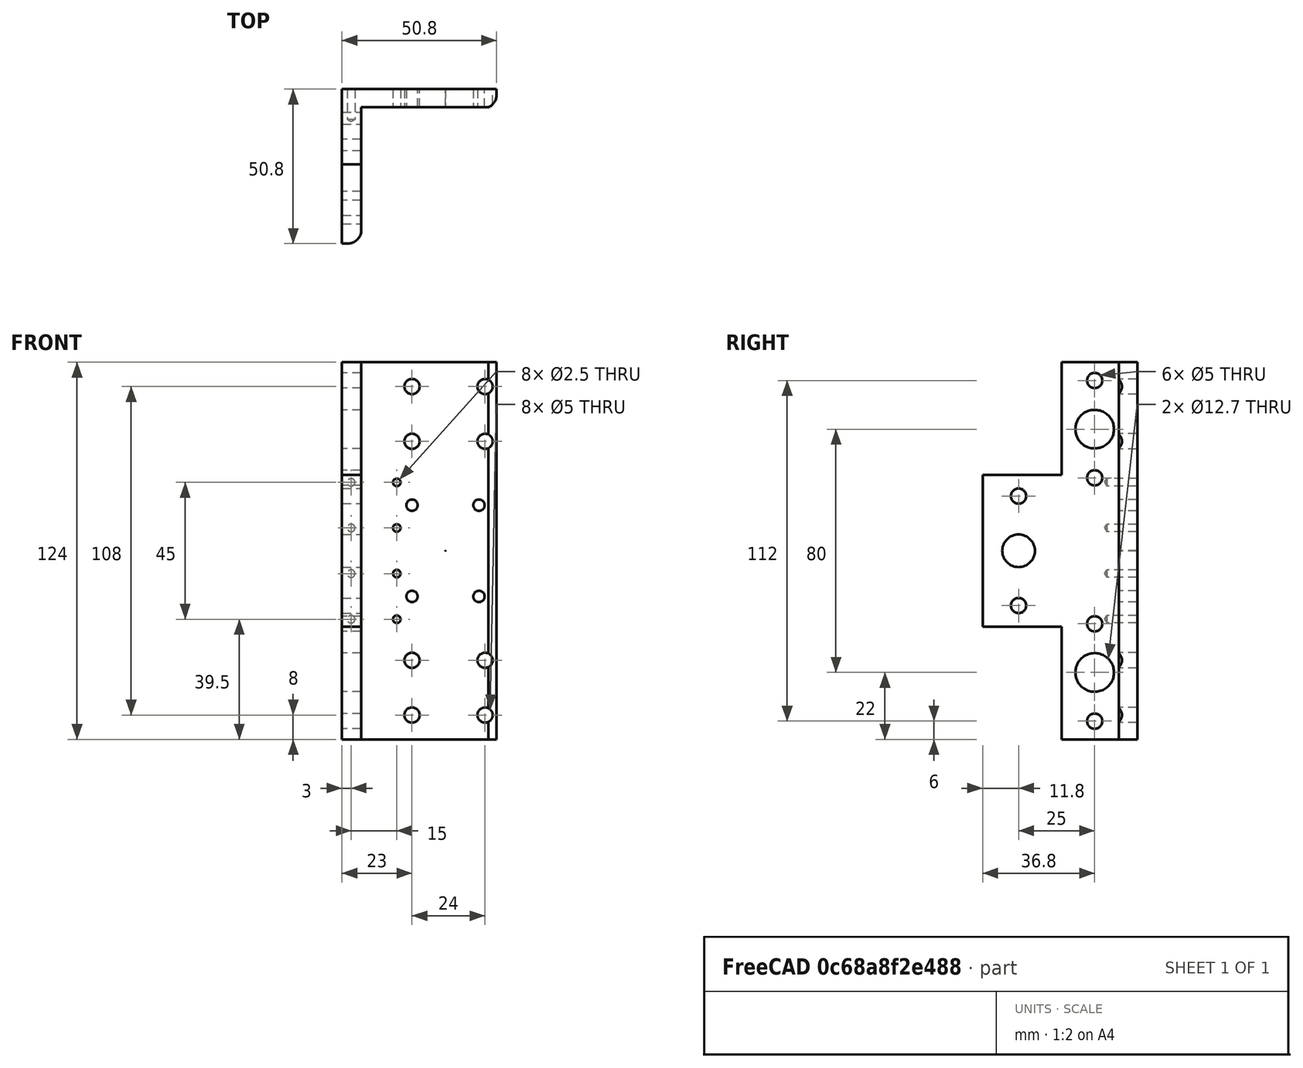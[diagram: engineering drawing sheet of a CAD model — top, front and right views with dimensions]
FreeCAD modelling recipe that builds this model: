
FCSTD DOCUMENT  (FreeCAD 0.19R)
Label: angle_machined_2in_25_drive_side
License: All rights reserved
LicenseURL: http://en.wikipedia.org/wiki/All_rights_reserved
objects: TechDraw::DrawViewDimension×26, PartDesign::CoordinateSystem×17, Sketcher::SketchObject×9, PartDesign::Pocket×7, PartDesign::Mirrored×3, TechDraw::DrawViewPart×3, PartDesign::Pad×2, PartDesign::Fillet×1, PartDesign::LinearPattern×1, PartDesign::Hole×1, PartDesign::Body×1, TechDraw::DrawSVGTemplate×1, TechDraw::DrawViewAnnotation×1, TechDraw::DrawPage×1
note: 53 computed .brp shape members not serialized (recipe doc carries the construction recipe); baked Part::Feature solids carry a one-line shape summary decoded from their .brp

FEATURE [Sketcher::SketchObject] Sketch
  FullyConstrained = true
  MapMode = 5
  Support = -> [XY_Plane]
  sketch-geometry (6):
    g0: LineSegment StartX=0 StartY=0 StartZ=0 EndX=50.8 EndY=0 EndZ=0
    g1: LineSegment StartX=50.8 StartY=0 StartZ=0 EndX=50.8 EndY=-6.35 EndZ=0
    g2: LineSegment StartX=50.8 StartY=-6.35 StartZ=0 EndX=6.35 EndY=-6.35 EndZ=0
    g3: LineSegment StartX=6.35 StartY=-6.35 StartZ=0 EndX=6.35 EndY=-50.8 EndZ=0
    g4: LineSegment StartX=6.35 StartY=-50.8 StartZ=0 EndX=0 EndY=-50.8 EndZ=0
    g5: LineSegment StartX=0 StartY=-50.8 StartZ=0 EndX=0 EndY=0 EndZ=0
  constraints (17):
    c: Coincident(g-1,g0)
    c: PointOnObject(g0,g-1)
    c: Coincident(g0,g1)
    c: Vertical(g1)
    c: Coincident(g1,g2)
    c: Horizontal(g2)
    c: Coincident(g2,g3)
    c: Vertical(g3)
    c: Coincident(g3,g4)
    c: PointOnObject(g4,g-2)
    c: Horizontal(g4)
    c: Coincident(g4,g5)
    c: Coincident(g5,g0)
    c: Equal(g1,g4)
    c: DistanceY(g1,g1) = 6.35
    c: DistanceX(g0,g0) = 50.8
    c: Equal(g0,g5)
FEATURE [PartDesign::Pad] Pad
  Direction = (1,1,1)
  Length = 62
  Length2 = 100
  Profile = -> Sketch
  Refine = true
  Reversed = true
  Type = 0
FEATURE [Sketcher::SketchObject] Sketch001
  FullyConstrained = true
  MapMode = 5
  Placement = pos=(0,0,0) rot=(0.57735,0.57735,0.57735;2.0944rad)
  Support = -> [YZ_Plane]
  sketch-geometry (3):
    g0: Circle CenterX=-14 CenterY=-40 CenterZ=0 NormalX=0 NormalY=0 NormalZ=1 AngleXU=0 Radius=6.35
    g1: Circle CenterX=-14 CenterY=-24 CenterZ=0 NormalX=0 NormalY=0 NormalZ=1 AngleXU=0 Radius=2.5
    g2: Circle CenterX=-14 CenterY=-56 CenterZ=0 NormalX=0 NormalY=0 NormalZ=1 AngleXU=0 Radius=2.5
  constraints (8):
    c: Diameter(g0) = 12.7
    c: Diameter(g1) = 5
    c: Equal(g1,g2)
    c: Symmetric(g1,g2,g0)
    c: Vertical(g1,g0)
    c: Distance(g1,g2) = 32
    c: DistanceX(g0,g-1) = 14
    c: DistanceY(g0,g-1) = 40
FEATURE [Sketcher::SketchObject] Sketch002
  FullyConstrained = true
  MapMode = 5
  Placement = pos=(0,0,0) rot=(0.57735,0.57735,0.57735;2.0944rad)
  Support = -> [YZ_Plane]
  sketch-geometry (3):
    g0: Circle CenterX=-39 CenterY=0 CenterZ=0 NormalX=0 NormalY=0 NormalZ=1 AngleXU=0 Radius=5.35781
    g1: Circle CenterX=-39 CenterY=18 CenterZ=0 NormalX=0 NormalY=0 NormalZ=1 AngleXU=0 Radius=2.5
    g2: Circle CenterX=-39 CenterY=-18 CenterZ=0 NormalX=0 NormalY=0 NormalZ=1 AngleXU=0 Radius=2.5
  constraints (8):
    c: Diameter(g0) = 10.7156
    c: Horizontal(g0,g-1)
    c: Vertical(g1,g0)
    c: Diameter(g1) = 5
    c: Equal(g1,g2)
    c: Symmetric(g1,g2,g0)
    c: DistanceY(g2,g1) = 36
    c: DistanceX(g1,g-1) = 39
FEATURE [Sketcher::SketchObject] Sketch003
  FullyConstrained = true
  MapMode = 5
  Placement = pos=(0,0,0) rot=(1,0,0;1.5708rad)
  Support = -> [XZ_Plane]
  sketch-geometry (4):
    g0: LineSegment StartX=6.35 StartY=251.119 StartZ=0 EndX=66.35 EndY=251.119 EndZ=0
    g1: LineSegment StartX=66.35 StartY=251.119 StartZ=0 EndX=66.35 EndY=200 EndZ=0
    g2: LineSegment StartX=66.35 StartY=200 StartZ=0 EndX=6.35 EndY=200 EndZ=0
    g3: LineSegment StartX=6.35 StartY=200 StartZ=0 EndX=6.35 EndY=251.119 EndZ=0
  constraints (12):
    c: Coincident(g0,g1)
    c: Coincident(g1,g2)
    c: Coincident(g2,g3)
    c: Coincident(g3,g0)
    c: Horizontal(g0)
    c: Horizontal(g2)
    c: Vertical(g1)
    c: Vertical(g3)
    c: DistanceY(g3,g3) = 51.1187
    c: DistanceY(g-1,g2) = 200
    c: DistanceX(g0,g0) = 60
    c: DistanceX(g-1,g0) = 6.35
FEATURE [Sketcher::SketchObject] Sketch004
  FullyConstrained = true
  MapMode = 5
  Placement = pos=(0,0,0) rot=(1,0,0;1.5708rad)
  Support = -> [XZ_Plane]
  sketch-geometry (7):
    g0: Circle CenterX=45 CenterY=15 CenterZ=0 NormalX=0 NormalY=0 NormalZ=1 AngleXU=0 Radius=1.865
    g1: Circle CenterX=45 CenterY=-15 CenterZ=0 NormalX=0 NormalY=0 NormalZ=1 AngleXU=0 Radius=1.865
    g2: Circle CenterX=23 CenterY=15 CenterZ=0 NormalX=0 NormalY=0 NormalZ=1 AngleXU=0 Radius=1.865
    g3: Circle CenterX=23 CenterY=-15 CenterZ=0 NormalX=0 NormalY=0 NormalZ=1 AngleXU=0 Radius=1.865
    g4: LineSegment StartX=0 StartY=0 StartZ=0 EndX=-20.31 EndY=0 EndZ=0
    g5: LineSegment StartX=34 StartY=0 StartZ=0 EndX=34 EndY=70 EndZ=0
    g6: Circle CenterX=34 CenterY=0 CenterZ=0 NormalX=0 NormalY=0 NormalZ=1 AngleXU=0 Radius=0.05
  constraints (18):
    c: Horizontal(g4)
    c: Coincident(g4,g-1)
    c: Distance(g4) = 20.31
    c: Vertical(g5)
    c: Horizontal(g5,g-1)
    c: Symmetric(g2,g0,g5)
    c: Symmetric(g2,g3,g4)
    c: Symmetric(g0,g1,g4)
    c: DistanceX(g2,g0) = 22
    c: Equal(g2,g0)
    c: Equal(g1,g0)
    c: Equal(g1,g3)
    c: Diameter(g0) = 3.73
    c: DistanceY(g1,g0) = 30
    c: DistanceX(g-1,g5) = 34  'motor_x'
    c: DistanceY(g5,g5) = 70
    c: Coincident(g6,g5)
    c: Diameter(g6) = 0.1
FEATURE [PartDesign::Pad] Pad001
  BaseFeature = -> Pad
  Direction = (1,1,1)
  Length = 62
  Length2 = 100
  Profile = -> Sketch
  Refine = true
  Type = 0
FEATURE [PartDesign::Fillet] Fillet
  Base = -> Pad001 [Edge17,Edge18,Edge16]
  BaseFeature = -> Pad001
  Radius = 4.5
  Refine = true
  SupportTransform = false
FEATURE [PartDesign::Pocket] Pocket  label="top_bearing"
  BaseFeature = -> Fillet
  Length = 20
  Length2 = 100
  Profile = -> Sketch001
  Refine = true
  Reversed = true
  Type = 1
FEATURE [PartDesign::LinearPattern] LinearPattern  label="LinearPattern_lower_bearing"
  BaseFeature = -> Pocket
  Direction = -> Sketch001 [V_Axis]
  Length = 80
  Occurrences = 2
  Originals = -> [Pocket]
  Refine = true
FEATURE [PartDesign::Pocket] Pocket001  label="drive_hole_clearance"
  BaseFeature = -> LinearPattern
  Length = 5
  Length2 = 100
  Midplane = true
  Profile = -> Sketch002
  Refine = true
  Reversed = true
  Type = 1
FEATURE [PartDesign::Pocket] Pocket002  label="gross_cut"
  BaseFeature = -> Pocket001
  Length = 5
  Length2 = 100
  Midplane = true
  Profile = -> Sketch003
  Refine = true
  Type = 1
FEATURE [PartDesign::Mirrored] Mirrored001
  BaseFeature = -> Pocket002
  MirrorPlane = -> Sketch003 [H_Axis]
  Originals = -> [Pocket002]
  Refine = true
FEATURE [PartDesign::Pocket] Pocket003
  BaseFeature = -> Mirrored001
  Length = 5
  Length2 = 100
  Midplane = true
  Profile = -> Sketch004
  Type = 1
FEATURE [Sketcher::SketchObject] Sketch005
  FullyConstrained = true
  MapMode = 5
  Support = -> [XY_Plane]
  sketch-geometry (4):
    g0: LineSegment StartX=6.35 StartY=-6 StartZ=0 EndX=66.35 EndY=-6 EndZ=0
    g1: LineSegment StartX=66.35 StartY=-6 StartZ=0 EndX=66.35 EndY=-18.25 EndZ=0
    g2: LineSegment StartX=66.35 StartY=-18.25 StartZ=0 EndX=6.35 EndY=-18.25 EndZ=0
    g3: LineSegment StartX=6.35 StartY=-18.25 StartZ=0 EndX=6.35 EndY=-6 EndZ=0
  constraints (12):
    c: Coincident(g0,g1)
    c: Coincident(g1,g2)
    c: Coincident(g2,g3)
    c: Coincident(g3,g0)
    c: Horizontal(g0)
    c: Horizontal(g2)
    c: Vertical(g1)
    c: Vertical(g3)
    c: DistanceY(g1,g1) = 12.25
    c: DistanceX(g0,g0) = 60
    c: DistanceX(g-1,g0) = 6.35
    c: DistanceY(g0,g-1) = 6
FEATURE [PartDesign::Pocket] Pocket004
  BaseFeature = -> Pocket003
  Length = 5
  Length2 = 100
  Midplane = true
  Profile = -> Sketch005
  Refine = true
  Type = 1
FEATURE [Sketcher::SketchObject] Sketch006
  FullyConstrained = true
  MapMode = 5
  Placement = pos=(0,0,0) rot=(0.57735,0.57735,0.57735;2.0944rad)
  Support = -> [YZ_Plane]
  sketch-geometry (4):
    g0: LineSegment StartX=-62.1666 StartY=69.7638 StartZ=0 EndX=-24.8 EndY=69.7638 EndZ=0
    g1: LineSegment StartX=-24.8 StartY=69.7638 StartZ=0 EndX=-24.8 EndY=25 EndZ=0
    g2: LineSegment StartX=-24.8 StartY=25 StartZ=0 EndX=-62.1666 EndY=25 EndZ=0
    g3: LineSegment StartX=-62.1666 StartY=25 StartZ=0 EndX=-62.1666 EndY=69.7638 EndZ=0
  constraints (12):
    c: Coincident(g0,g1)
    c: Coincident(g1,g2)
    c: Coincident(g2,g3)
    c: Coincident(g3,g0)
    c: Horizontal(g0)
    c: Horizontal(g2)
    c: Vertical(g1)
    c: Vertical(g3)
    c: DistanceX(g0,g-1) = 24.8
    c: DistanceY(g-1,g1) = 25
    c: DistanceX(g2,g2) = 37.3666
    c: DistanceY(g3,g3) = 44.7638
FEATURE [PartDesign::Pocket] Pocket005
  BaseFeature = -> Pocket004
  Length = 5
  Length2 = 100
  Midplane = true
  Profile = -> Sketch006
  Refine = true
  Type = 1
FEATURE [PartDesign::Mirrored] Mirrored
  BaseFeature = -> Pocket005
  MirrorPlane = -> Sketch006 [H_Axis]
  Originals = -> [Pocket005]
  Refine = true
FEATURE [PartDesign::CoordinateSystem] Local_CS007  label="lcs_NUT"
  AttacherType = Attacher::AttachEngine3D
  MapMode = 11
  Placement = pos=(6.35,-39,1.81e-14) rot=(0.707107,0,0.707107;3.14159rad)
  Support = -> [Mirrored]
FEATURE [Sketcher::SketchObject] Sketch007
  FullyConstrained = true
  MapMode = 5
  Placement = pos=(0,0,0) rot=(1,0,0;1.5708rad)
  Support = -> [XZ_Plane]
  sketch-geometry (5):
    g0: Circle CenterX=23 CenterY=54 CenterZ=0 NormalX=0 NormalY=0 NormalZ=1 AngleXU=0 Radius=2.5
    g1: Circle CenterX=47 CenterY=54 CenterZ=0 NormalX=0 NormalY=0 NormalZ=1 AngleXU=0 Radius=2.5
    g2: Circle CenterX=47 CenterY=36 CenterZ=0 NormalX=0 NormalY=0 NormalZ=1 AngleXU=0 Radius=2.5
    g3: Circle CenterX=23 CenterY=36 CenterZ=0 NormalX=0 NormalY=0 NormalZ=1 AngleXU=0 Radius=2.5
    g4: GeomPoint X=35 Y=45 Z=0
  constraints (13):
    c: Vertical(g0,g3)
    c: Horizontal(g1,g0)
    c: Horizontal(g2,g3)
    c: Vertical(g2,g1)
    c: DistanceX(g0,g1) = 24
    c: DistanceY(g2,g1) = 18
    c: Equal(g1,g2)
    c: Equal(g2,g3)
    c: Equal(g3,g0)
    c: Diameter(g1) = 5
    c: Symmetric(g3,g1,g4)
    c: DistanceY(g-1,g4) = 45  'y1'
    c: DistanceX(g-1,g4) = 35  'x1'
FEATURE [PartDesign::Pocket] Pocket006  label="bearing_holes"
  BaseFeature = -> Mirrored
  Length = 5
  Length2 = 100
  Midplane = true
  Profile = -> Sketch007
  Refine = true
  Type = 1
FEATURE [PartDesign::Mirrored] Mirrored002
  BaseFeature = -> Pocket006
  MirrorPlane = -> Sketch007 [H_Axis]
  Originals = -> [Pocket006]
  Refine = true
FEATURE [PartDesign::CoordinateSystem] Local_CS
  AttacherType = Attacher::AttachEngine3D
  MapMode = 11
  Placement = pos=(47,0,54) rot=(0.57735,-0.57735,0.57735;2.0944rad)
  Support = -> [Mirrored002]
FEATURE [PartDesign::CoordinateSystem] Local_CS009
  AttacherType = Attacher::AttachEngine3D
  MapMode = 11
  Placement = pos=(23,0,-36) rot=(0.57735,-0.57735,0.57735;2.0944rad)
  Support = -> [Mirrored002]
FEATURE [PartDesign::CoordinateSystem] Local_CS010
  AttacherType = Attacher::AttachEngine3D
  MapMode = 11
  Placement = pos=(45,0,15) rot=(0.57735,-0.57735,0.57735;2.0944rad)
  Support = -> [Mirrored002]
FEATURE [PartDesign::CoordinateSystem] Local_CS011
  AttacherType = Attacher::AttachEngine3D
  MapMode = 11
  Placement = pos=(23,3.3e-15,-15) rot=(0.57735,-0.57735,0.57735;2.0944rad)
  Support = -> [Sketch004]
FEATURE [PartDesign::CoordinateSystem] Local_CS012
  AttacherType = Attacher::AttachEngine3D
  MapMode = 11
  Placement = pos=(47,0,-54) rot=(0.57735,-0.57735,0.57735;2.0944rad)
  Support = -> [Mirrored002]
FEATURE [PartDesign::CoordinateSystem] Local_CS013
  AttacherType = Attacher::AttachEngine3D
  MapMode = 11
  Placement = pos=(23,0,15) rot=(0.57735,-0.57735,0.57735;2.0944rad)
  Support = -> [Mirrored002]
FEATURE [PartDesign::CoordinateSystem] Local_CS015
  AttacherType = Attacher::AttachEngine3D
  MapMode = 11
  Placement = pos=(6.35,-14,56) rot=(0.707107,0,-0.707107;3.14159rad)
  Support = -> [Mirrored002]
FEATURE [PartDesign::CoordinateSystem] Local_CS016
  AttacherType = Attacher::AttachEngine3D
  MapMode = 11
  Placement = pos=(6.35,-14,24) rot=(0.707107,0,-0.707107;3.14159rad)
  Support = -> [Mirrored002]
FEATURE [PartDesign::CoordinateSystem] Local_CS017
  AttacherType = Attacher::AttachEngine3D
  MapMode = 11
  Placement = pos=(6.35,-14,-24) rot=(0.707107,0,-0.707107;3.14159rad)
  Support = -> [Mirrored002]
FEATURE [PartDesign::CoordinateSystem] Local_CS018
  AttacherType = Attacher::AttachEngine3D
  MapMode = 11
  Placement = pos=(6.35,-14,-56) rot=(0.707107,0,-0.707107;3.14159rad)
  Support = -> [Mirrored002]
FEATURE [PartDesign::CoordinateSystem] Local_CS019
  AttacherType = Attacher::AttachEngine3D
  MapMode = 11
  Placement = pos=(-1.8e-14,-14,56) rot=(0.707107,0,0.707107;3.14159rad)
  Support = -> [Mirrored002]
FEATURE [PartDesign::CoordinateSystem] Local_CS020
  AttacherType = Attacher::AttachEngine3D
  MapMode = 11
  Placement = pos=(-1.8e-14,-14,24) rot=(0.707107,0,0.707107;3.14159rad)
  Support = -> [Mirrored002]
FEATURE [PartDesign::CoordinateSystem] Local_CS021
  AttacherType = Attacher::AttachEngine3D
  MapMode = 11
  Placement = pos=(0,-14,-24) rot=(0.707107,0,0.707107;3.14159rad)
  Support = -> [Mirrored002]
FEATURE [PartDesign::CoordinateSystem] Local_CS022
  AttacherType = Attacher::AttachEngine3D
  MapMode = 11
  Placement = pos=(0,-14,-56) rot=(0.707107,0,0.707107;3.14159rad)
  Support = -> [Mirrored002]
FEATURE [Sketcher::SketchObject] Sketch008
  FullyConstrained = true
  MapMode = 5
  Placement = pos=(0,0,0) rot=(0,0.707107,0.707107;3.14159rad)
  Support = -> [Mirrored002]
  sketch-geometry (8):
    g0: Circle CenterX=-18 CenterY=-7.5 CenterZ=0 NormalX=0 NormalY=0 NormalZ=1 AngleXU=0 Radius=1
    g1: Circle CenterX=-3 CenterY=-7.5 CenterZ=0 NormalX=0 NormalY=0 NormalZ=1 AngleXU=0 Radius=1
    g2: Circle CenterX=-3 CenterY=-22.5 CenterZ=0 NormalX=0 NormalY=0 NormalZ=1 AngleXU=0 Radius=1
    g3: Circle CenterX=-18 CenterY=-22.5 CenterZ=0 NormalX=0 NormalY=0 NormalZ=1 AngleXU=0 Radius=1
    g4: Circle CenterX=-3 CenterY=7.5 CenterZ=0 NormalX=0 NormalY=0 NormalZ=1 AngleXU=0 Radius=1
    g5: Circle CenterX=-3 CenterY=22.5 CenterZ=0 NormalX=0 NormalY=0 NormalZ=1 AngleXU=0 Radius=1
    g6: Circle CenterX=-18 CenterY=22.5 CenterZ=0 NormalX=0 NormalY=0 NormalZ=1 AngleXU=0 Radius=1
    g7: Circle CenterX=-18 CenterY=7.5 CenterZ=0 NormalX=0 NormalY=0 NormalZ=1 AngleXU=0 Radius=1
  constraints (20):
    c: Equal(g2,g1)
    c: Equal(g0,g1)
    c: Equal(g3,g0)
    c: DistanceX(g3,g2) = 15
    c: DistanceY(g2,g1) = 15
    c: Horizontal(g2,g3)
    c: Diameter(g0) = 2
    c: DistanceX(g1,g-1) = 3
    c: Horizontal(g1,g0)
    c: Vertical(g3,g0)
    c: Vertical(g1,g2)
    c: DistanceY(g1,g-1) = 7.5
    c: Symmetric(g1,g4,g-1)
    c: Symmetric(g0,g7,g-1)
    c: Symmetric(g2,g5,g-1)
    c: Symmetric(g6,g3,g-1)
    c: Equal(g4,g7)
    c: Equal(g5,g4)
    c: Equal(g5,g6)
    c: Equal(g3,g6)
FEATURE [PartDesign::Hole] Hole
  BaseFeature = -> Mirrored002
  Depth = 10
  DepthType = 0
  Diameter = 2.5
  DrillForDepth = false
  DrillPoint = 1
  DrillPointAngle = 118
  HoleCutCountersinkAngle = 90
  HoleCutCustomValues = false
  HoleCutDepth = 3.4
  HoleCutDiameter = 6.1
  HoleCutType = 0
  ModelActualThread = false
  Profile = -> Sketch008
  Refine = true
  Tapered = false
  TaperedAngle = 90
  ThreadAngle = 60
  ThreadClass = 0
  ThreadCutOffInner = 0.0541266
  ThreadCutOffOuter = 0.108253
  ThreadDirection = 0
  ThreadFit = 1
  ThreadPitch = 0.5
  ThreadSize = 9
  ThreadType = 1
  Threaded = true
FEATURE [PartDesign::CoordinateSystem] Local_CS023
  AttacherType = Attacher::AttachEngine3D
  MapMode = 5
  Placement = pos=(0,0,0) rot=(0,0.707107,0.707107;3.14159rad)
  Support = -> [Hole]
FEATURE [PartDesign::CoordinateSystem] Local_CS025
  AttacherType = Attacher::AttachEngine3D
  MapMode = 11
  Placement = pos=(3,-5e-15,-22.5) rot=(0.57735,-0.57735,-0.57735;4.18879rad)
  Support = -> [Hole]
FEATURE [PartDesign::Body] Body
  Group = -> [Sketch,Pad,Pad001,Sketch001,Fillet,Pocket,Sketch002,LinearPattern,Pocket001,Sketch003,Pocket002,Mirrored001,Sketch004,Pocket003,Sketch005,Pocket004,Sketch006,Pocket005,Mirrored,Local_CS007,Sketch007,Pocket006,Mirrored002,Local_CS,Local_CS009,Local_CS010,Local_CS011,Local_CS012,Local_CS013,Local_CS015,Local_CS016,Local_CS017,Local_CS018,Local_CS019,Local_CS020,Local_CS021,Local_CS022,Sketch008,+3 more]
  Origin = -> Origin
  Tip = -> Hole
FEATURE [TechDraw::DrawSVGTemplate] Template
  EditableTexts = 1 : 4=1:2; 99=1; 99 - MM=1; DRAWING NO.=DRAWING NO.; Titel / zusätzliche Informationen=test; YYYY-MM-DD=2020-10-06
  Height = 210
  Orientation = 1
  Width = 297
FEATURE [TechDraw::DrawViewPart] View  label=" "
  CoarseView = false
  Direction = (0,1,0)
  Focus = 100
  HardHidden = false
  IsoCount = 0
  IsoHidden = false
  IsoVisible = false
  LockPosition = true
  Perspective = false
  Rotation = 0
  Scale = 0.5
  ScaleType = 0
  SeamHidden = false
  SeamVisible = true
  SmoothHidden = false
  SmoothVisible = true
  Source = -> [Body]
  X = 134.439
  XDirection = (-1,0,0)
  Y = 108
FEATURE [TechDraw::DrawViewDimension] Dimension
  Arbitrary = false
  ArbitraryTolerances = false
  EqualTolerance = true
  FormatSpec = %.0f
  FormatSpecOverTolerance = %+.0f
  FormatSpecUnderTolerance = %+.0f
  Inverted = false
  LockPosition = false
  MeasureType = 1
  OverTolerance = 0
  References2D = -> [View]
  Rotation = 0
  Scale = 0.5
  ScaleType = 0
  TheoreticalExact = false
  Type = 1
  UnderTolerance = 0
  X = 8.68058
  Y = 60.3564
FEATURE [TechDraw::DrawViewDimension] Dimension002
  Arbitrary = false
  ArbitraryTolerances = false
  EqualTolerance = true
  FormatSpec = %.0f
  FormatSpecOverTolerance = %+.0f
  FormatSpecUnderTolerance = %+.0f
  Inverted = false
  LockPosition = false
  MeasureType = 1
  OverTolerance = 0
  References2D = -> [View]
  Rotation = 0
  Scale = 0.5
  ScaleType = 0
  TheoreticalExact = false
  Type = 2
  UnderTolerance = 0
  X = -65.2145
  Y = 0.08206
FEATURE [TechDraw::DrawViewDimension] Dimension003
  Arbitrary = false
  ArbitraryTolerances = false
  EqualTolerance = true
  FormatSpec = %.0f
  FormatSpecOverTolerance = %+.0f
  FormatSpecUnderTolerance = %+.0f
  Inverted = false
  LockPosition = false
  MeasureType = 1
  OverTolerance = 0
  References2D = -> [View]
  Rotation = 0
  Scale = 0.5
  ScaleType = 0
  TheoreticalExact = false
  Type = 2
  UnderTolerance = 0
  X = -27.5176
  Y = 41.8447
FEATURE [TechDraw::DrawViewPart] View001
  CoarseView = false
  Direction = (-0.577,0.577,0.577)
  Focus = 100
  HardHidden = false
  IsoCount = 0
  IsoHidden = false
  IsoVisible = false
  LockPosition = false
  Perspective = false
  Rotation = 0
  Scale = 0.5
  ScaleType = 0
  SeamHidden = false
  SeamVisible = true
  SmoothHidden = false
  SmoothVisible = true
  Source = -> [Body]
  X = 36.4593
  XDirection = (-0.707,-0.707,0)
  Y = 151.571
FEATURE [TechDraw::DrawViewPart] View002  label="  "
  CoarseView = false
  Direction = (-1,0,0)
  Focus = 100
  HardHidden = false
  IsoCount = 0
  IsoHidden = false
  IsoVisible = false
  LockPosition = true
  Perspective = false
  Rotation = 0
  Scale = 0.5
  ScaleType = 0
  SeamHidden = false
  SeamVisible = true
  SmoothHidden = false
  SmoothVisible = true
  Source = -> [Body]
  X = 220
  XDirection = (0,-1,0)
  Y = 108
FEATURE [TechDraw::DrawViewDimension] Dimension004
  Arbitrary = false
  ArbitraryTolerances = false
  EqualTolerance = true
  FormatSpec = %.0f
  FormatSpecOverTolerance = %+.0f
  FormatSpecUnderTolerance = %+.0f
  Inverted = false
  LockPosition = false
  MeasureType = 1
  OverTolerance = 0
  References2D = -> [View]
  Rotation = 0
  Scale = 0.5
  ScaleType = 0
  TheoreticalExact = false
  Type = 2
  UnderTolerance = 0
  X = -36.0722
  Y = 15.3836
FEATURE [TechDraw::DrawViewDimension] Dimension005
  Arbitrary = false
  ArbitraryTolerances = false
  EqualTolerance = true
  FormatSpec = ⌀%.0f
  FormatSpecOverTolerance = %+.0f
  FormatSpecUnderTolerance = %+.0f
  Inverted = false
  LockPosition = false
  MeasureType = 1
  OverTolerance = 0
  References2D = -> [View]
  Rotation = 0
  Scale = 0.5
  ScaleType = 0
  TheoreticalExact = false
  Type = 5
  UnderTolerance = 0
  X = 7.8661
  Y = 39.6018
FEATURE [TechDraw::DrawViewDimension] Dimension006
  Arbitrary = false
  ArbitraryTolerances = false
  EqualTolerance = true
  FormatSpec = %.0f
  FormatSpecOverTolerance = %+.0f
  FormatSpecUnderTolerance = %+.0f
  Inverted = false
  LockPosition = false
  MeasureType = 1
  OverTolerance = 0
  References2D = -> [View]
  Rotation = 0
  Scale = 0.5
  ScaleType = 0
  TheoreticalExact = false
  Type = 2
  UnderTolerance = 0
  X = -30.8384
  Y = -7.25973
FEATURE [TechDraw::DrawViewDimension] Dimension007
  Arbitrary = false
  ArbitraryTolerances = false
  EqualTolerance = true
  FormatSpec = %.0f
  FormatSpecOverTolerance = %+.0f
  FormatSpecUnderTolerance = %+.0f
  Inverted = false
  LockPosition = false
  MeasureType = 1
  OverTolerance = 0
  References2D = -> [View]
  Rotation = 0
  Scale = 0.5
  ScaleType = 0
  TheoreticalExact = false
  Type = 2
  UnderTolerance = 0
  X = 38.0639
  Y = 20.3537
FEATURE [TechDraw::DrawViewDimension] Dimension008
  Arbitrary = false
  ArbitraryTolerances = false
  EqualTolerance = true
  FormatSpec = %.0f
  FormatSpecOverTolerance = %+.0f
  FormatSpecUnderTolerance = %+.0f
  Inverted = false
  LockPosition = false
  MeasureType = 1
  OverTolerance = 0
  References2D = -> [View]
  Rotation = 0
  Scale = 0.5
  ScaleType = 0
  TheoreticalExact = false
  Type = 1
  UnderTolerance = 0
  X = 25.4362
  Y = 18.7897
FEATURE [TechDraw::DrawViewDimension] Dimension010
  Arbitrary = false
  ArbitraryTolerances = false
  EqualTolerance = true
  FormatSpec = ⌀%.0f
  FormatSpecOverTolerance = %+.0f
  FormatSpecUnderTolerance = %+.0f
  Inverted = false
  LockPosition = false
  MeasureType = 1
  OverTolerance = 0
  References2D = -> [View]
  Rotation = 0
  Scale = 0.5
  ScaleType = 0
  TheoreticalExact = false
  Type = 5
  UnderTolerance = 0
  X = -23.0747
  Y = 6.9067
FEATURE [TechDraw::DrawViewDimension] Dimension011
  Arbitrary = false
  ArbitraryTolerances = false
  EqualTolerance = true
  FormatSpec = %.0f
  FormatSpecOverTolerance = %+.0f
  FormatSpecUnderTolerance = %+.0f
  Inverted = false
  LockPosition = false
  MeasureType = 1
  OverTolerance = 0
  References2D = -> [View]
  Rotation = 0
  Scale = 0.5
  ScaleType = 0
  TheoreticalExact = false
  Type = 1
  UnderTolerance = 0
  X = 22.9041
  Y = 46.3177
FEATURE [TechDraw::DrawViewDimension] Dimension012
  Arbitrary = false
  ArbitraryTolerances = false
  EqualTolerance = true
  FormatSpec = %.0f
  FormatSpecOverTolerance = %+.0f
  FormatSpecUnderTolerance = %+.0f
  Inverted = false
  LockPosition = false
  MeasureType = 1
  OverTolerance = 0
  References2D = -> [View]
  Rotation = 0
  Scale = 0.5
  ScaleType = 0
  TheoreticalExact = false
  Type = 1
  UnderTolerance = 0
  X = 26.2559
  Y = 28.0765
FEATURE [TechDraw::DrawViewDimension] Dimension013
  Arbitrary = false
  ArbitraryTolerances = false
  EqualTolerance = true
  FormatSpec = %.1f
  FormatSpecOverTolerance = %+.1f
  FormatSpecUnderTolerance = %+.1f
  Inverted = false
  LockPosition = false
  MeasureType = 1
  OverTolerance = 0
  References2D = -> [View]
  Rotation = 0
  Scale = 0.5
  ScaleType = 0
  TheoreticalExact = false
  Type = 2
  UnderTolerance = 0
  X = 45.81
  Y = -8.63325
FEATURE [TechDraw::DrawViewDimension] Dimension014
  Arbitrary = false
  ArbitraryTolerances = false
  EqualTolerance = true
  FormatSpec = ⌀%.1f
  FormatSpecOverTolerance = %+.1f
  FormatSpecUnderTolerance = %+.1f
  Inverted = false
  LockPosition = false
  MeasureType = 1
  OverTolerance = 0
  References2D = -> [View]
  Rotation = 0
  Scale = 0.5
  ScaleType = 0
  TheoreticalExact = false
  Type = 5
  UnderTolerance = 0
  X = 26.2468
  Y = -11.3901
FEATURE [TechDraw::DrawViewAnnotation] Annotation  label="   "
  Font = osifont
  LineSpace = 80
  LockPosition = false
  MaxWidth = -1
  Rotation = 0
  Scale = 0.5
  ScaleType = 0
  Text = M3 X 0.5 | 10mm DEEP
  TextSize = 5
  TextStyle = 0
  X = 166.576
  Y = 81.2293
FEATURE [TechDraw::DrawViewDimension] Dimension015
  Arbitrary = false
  ArbitraryTolerances = false
  EqualTolerance = true
  FormatSpec = %.1f
  FormatSpecOverTolerance = %+.1f
  FormatSpecUnderTolerance = %+.1f
  Inverted = false
  LockPosition = false
  MeasureType = 1
  OverTolerance = 0
  References2D = -> [View002]
  Rotation = 0
  Scale = 0.5
  ScaleType = 0
  TheoreticalExact = false
  Type = 2
  UnderTolerance = 0
  X = 23.5075
  Y = 23.7232
FEATURE [TechDraw::DrawViewDimension] Dimension016
  Arbitrary = false
  ArbitraryTolerances = false
  EqualTolerance = true
  FormatSpec = %.1f
  FormatSpecOverTolerance = %+.1f
  FormatSpecUnderTolerance = %+.1f
  Inverted = false
  LockPosition = false
  MeasureType = 1
  OverTolerance = 0
  References2D = -> [View002]
  Rotation = 0
  Scale = 0.5
  ScaleType = 0
  TheoreticalExact = false
  Type = 2
  UnderTolerance = 0
  X = 37.0052
  Y = 1.43385
FEATURE [TechDraw::DrawViewDimension] Dimension017
  Arbitrary = false
  ArbitraryTolerances = false
  EqualTolerance = true
  FormatSpec = %.1f
  FormatSpecOverTolerance = %+.1f
  FormatSpecUnderTolerance = %+.1f
  Inverted = false
  LockPosition = false
  MeasureType = 1
  OverTolerance = 0
  References2D = -> [View002]
  Rotation = 0
  Scale = 0.5
  ScaleType = 0
  TheoreticalExact = false
  Type = 2
  UnderTolerance = 0
  X = -23.5122
  Y = 22.3882
FEATURE [TechDraw::DrawViewDimension] Dimension018
  Arbitrary = false
  ArbitraryTolerances = false
  EqualTolerance = true
  FormatSpec = %.1f
  FormatSpecOverTolerance = %+.1f
  FormatSpecUnderTolerance = %+.1f
  Inverted = false
  LockPosition = false
  MeasureType = 1
  OverTolerance = 0
  References2D = -> [View002]
  Rotation = 0
  Scale = 0.5
  ScaleType = 0
  TheoreticalExact = false
  Type = 1
  UnderTolerance = 0
  X = -27.0831
  Y = 40.3806
FEATURE [TechDraw::DrawViewDimension] Dimension019
  Arbitrary = false
  ArbitraryTolerances = false
  EqualTolerance = true
  FormatSpec = %.1f
  FormatSpecOverTolerance = %+.1f
  FormatSpecUnderTolerance = %+.1f
  Inverted = false
  LockPosition = false
  MeasureType = 1
  OverTolerance = 0
  References2D = -> [View002]
  Rotation = 0
  Scale = 0.5
  ScaleType = 0
  TheoreticalExact = false
  Type = 1
  UnderTolerance = 0
  X = -39.7478
  Y = 45.9113
FEATURE [TechDraw::DrawViewDimension] Dimension020
  Arbitrary = false
  ArbitraryTolerances = false
  EqualTolerance = true
  FormatSpec = ⌀%.1f
  FormatSpecOverTolerance = %+.1f
  FormatSpecUnderTolerance = %+.1f
  Inverted = false
  LockPosition = false
  MeasureType = 1
  OverTolerance = 0
  References2D = -> [View002]
  Rotation = 0
  Scale = 0.5
  ScaleType = 0
  TheoreticalExact = false
  Type = 5
  UnderTolerance = 0
  X = -24.4347
  Y = 9.38597
FEATURE [TechDraw::DrawViewDimension] Dimension021
  Arbitrary = false
  ArbitraryTolerances = false
  EqualTolerance = true
  FormatSpec = ⌀%.1f
  FormatSpecOverTolerance = %+.1f
  FormatSpecUnderTolerance = %+.1f
  Inverted = false
  LockPosition = false
  MeasureType = 1
  OverTolerance = 0
  References2D = -> [View002]
  Rotation = 0
  Scale = 0.5
  ScaleType = 0
  TheoreticalExact = false
  Type = 5
  UnderTolerance = 0
  X = -20.6124
  Y = -5.37424
FEATURE [TechDraw::DrawViewDimension] Dimension022
  Arbitrary = false
  ArbitraryTolerances = false
  EqualTolerance = true
  FormatSpec = ⌀%.1f
  FormatSpecOverTolerance = %+.1f
  FormatSpecUnderTolerance = %+.1f
  Inverted = false
  LockPosition = false
  MeasureType = 1
  OverTolerance = 0
  References2D = -> [View002]
  Rotation = 0
  Scale = 0.5
  ScaleType = 0
  TheoreticalExact = false
  Type = 5
  UnderTolerance = 0
  X = 0.376729
  Y = 37.4845
FEATURE [TechDraw::DrawViewDimension] Dimension023
  Arbitrary = false
  ArbitraryTolerances = false
  EqualTolerance = true
  FormatSpec = ⌀%.1f
  FormatSpecOverTolerance = %+.1f
  FormatSpecUnderTolerance = %+.1f
  Inverted = false
  LockPosition = false
  MeasureType = 1
  OverTolerance = 0
  References2D = -> [View002]
  Rotation = 0
  Scale = 0.5
  ScaleType = 0
  TheoreticalExact = false
  Type = 5
  UnderTolerance = 0
  X = 12.0279
  Y = 21.0011
FEATURE [TechDraw::DrawViewDimension] Dimension024
  Arbitrary = false
  ArbitraryTolerances = false
  EqualTolerance = true
  FormatSpec = %.1f
  FormatSpecOverTolerance = %+.1f
  FormatSpecUnderTolerance = %+.1f
  Inverted = false
  LockPosition = false
  MeasureType = 1
  OverTolerance = 0
  References2D = -> [View002]
  Rotation = 0
  Scale = 0.5
  ScaleType = 0
  TheoreticalExact = false
  Type = 1
  UnderTolerance = 0
  X = -0.247613
  Y = -34.0422
FEATURE [TechDraw::DrawViewDimension] Dimension025
  Arbitrary = false
  ArbitraryTolerances = false
  EqualTolerance = true
  FormatSpec = %.1f
  FormatSpecOverTolerance = %+.1f
  FormatSpecUnderTolerance = %+.1f
  Inverted = false
  LockPosition = false
  MeasureType = 1
  OverTolerance = 0
  References2D = -> [View]
  Rotation = 0
  Scale = 0.5
  ScaleType = 0
  TheoreticalExact = false
  Type = 1
  UnderTolerance = 0
  X = 0.325494
  Y = -45.6472
FEATURE [TechDraw::DrawViewDimension] Dimension026
  Arbitrary = false
  ArbitraryTolerances = false
  EqualTolerance = true
  FormatSpec = %.1f
  FormatSpecOverTolerance = %+.1f
  FormatSpecUnderTolerance = %+.1f
  Inverted = false
  LockPosition = false
  MeasureType = 1
  OverTolerance = 0
  References2D = -> [View002]
  Rotation = 0
  Scale = 0.5
  ScaleType = 0
  TheoreticalExact = false
  Type = 2
  UnderTolerance = 0
  X = 27.6849
  Y = -15.5
FEATURE [TechDraw::DrawViewDimension] Dimension027
  Arbitrary = false
  ArbitraryTolerances = false
  EqualTolerance = true
  FormatSpec = %.1f
  FormatSpecOverTolerance = %+.1f
  FormatSpecUnderTolerance = %+.1f
  Inverted = false
  LockPosition = false
  MeasureType = 1
  OverTolerance = 0
  References2D = -> [View002]
  Rotation = 0
  Scale = 0.5
  ScaleType = 0
  TheoreticalExact = false
  Type = 2
  UnderTolerance = 0
  X = -27.951
  Y = -10.529
FEATURE [TechDraw::DrawPage] Page
  KeepUpdated = true
  NextBalloonIndex = 1
  ProjectionType = 1
  Scale = 0.5
  Template = -> Template
  Views = -> [View,Dimension,Dimension002,Dimension003,View001,View002,Dimension004,Dimension005,Dimension006,Dimension007,Dimension008,Dimension010,Dimension011,Dimension012,Dimension013,Dimension014,Annotation,Dimension015,Dimension016,Dimension017,Dimension018,Dimension019,Dimension020,Dimension021,Dimension022,Dimension023,Dimension024,Dimension025,Dimension026,Dimension027]
